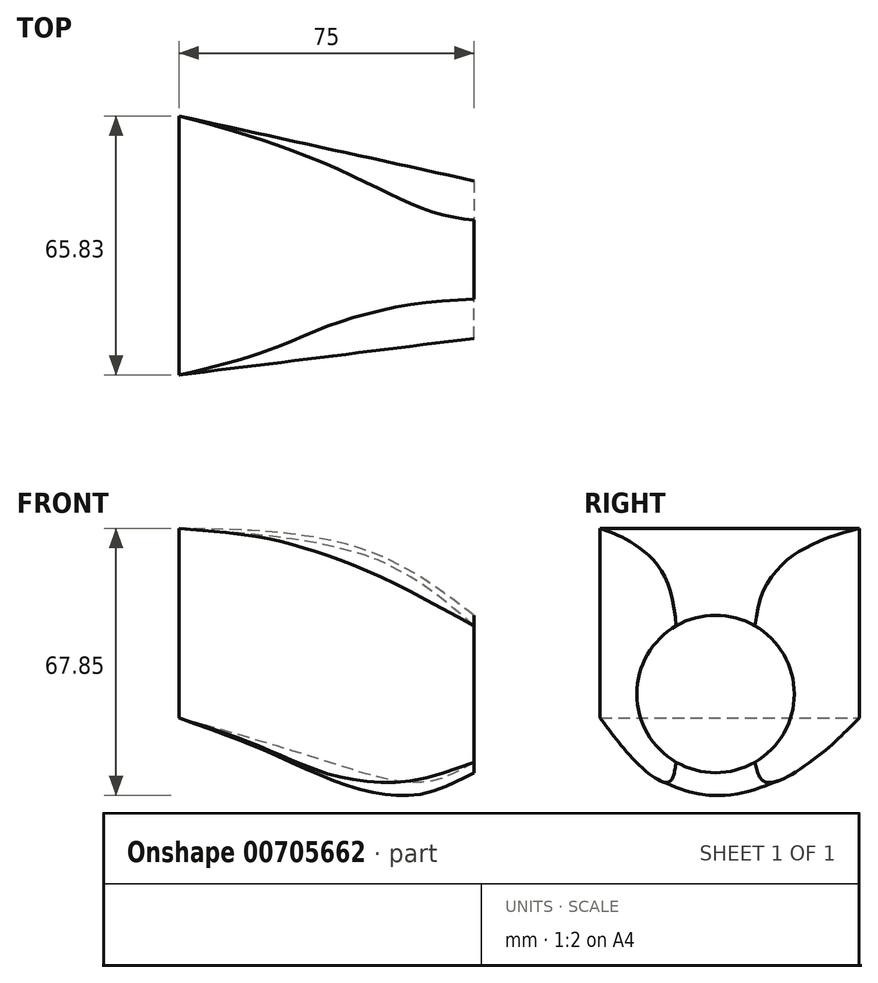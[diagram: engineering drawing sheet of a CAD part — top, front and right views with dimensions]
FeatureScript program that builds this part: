
annotation { "Feature Type Name" : "Feature", "Feature Type Description" : "" }
export const myFeature = defineFeature(function(context is Context, id is Id, definition is map)
    precondition{}
    {
        {
            var Q0;
            Q0=qCreatedBy(makeId("Right.planeOp"),FACE);
            var sketch = newSketch(context, id + "F0", { "sketchPlane" : qUnion([Q0])});
            skCircle(sketch, "E0", {"center": v(0, 0) * mm, "radius": 20 * mm});
            skSolve(sketch);
        }
        {
            var Q0;
            Q0=qCreatedBy(makeId("Right.planeOp"),FACE);
            cPlane(context, id + "F1", {"entities" : qUnion([Q0]), "cplaneType" : CPlaneType.OFFSET, "offset" : 75 * mm, "oppositeDirection" : true, "width" : 150 * mm, "height" : 150 * mm});
        }
        {
            var Q0;
            Q0=qCreatedBy(id+"F1.planeOp",FACE);
            var sketch = newSketch(context, id + "F2", { "sketchPlane" : qUnion([Q0])});
            skLineSegment(sketch, "E1.bottom", {"start": v(-29.32, -6.1) * mm, "end": v(36.51, -6.1) * mm});
            skLineSegment(sketch, "E1.top", {"start": v(-29.32, 42.04) * mm, "end": v(36.51, 42.04) * mm});
            skLineSegment(sketch, "E1.left", {"start": v(-29.32, -6.1) * mm, "end": v(-29.32, 42.04) * mm});
            skLineSegment(sketch, "E1.right", {"start": v(36.51, -6.1) * mm, "end": v(36.51, 42.04) * mm});
            skSolve(sketch);
        }
        {
            var Q0;
            Q0=qCreatedBy(makeId("Top.planeOp"),FACE);
            var sketch = newSketch(context, id + "F3", { "sketchPlane" : qUnion([Q0])});
            skLineSegment(sketch, "E2.0", {"start": v(-75, -29.32) * mm, "end": v(-75, 36.51) * mm});
            skLineSegment(sketch, "E3.0", {"start": v(0, 20) * mm, "end": v(0, -20) * mm});
            skPoint(sketch, "E4.2.internal.snap0", {"position": v(-75, 3.6) * mm});
            skFitSpline(sketch, "E4", {"points": [v(0, 0) * mm, v(-29.86, 13.64) * mm, v(-75, 0) * mm], "startDerivative": vector(-55.23, 57.64) * mm, "endDerivative": vector(-99.49, -65.42) * mm});
            skLineSegment(sketch, "E5", {"start": v(0, -20) * mm, "end": v(-75, -29.32) * mm});
            skLineSegment(sketch, "E6", {"start": v(0, 20) * mm, "end": v(-75, 36.51) * mm});
            skSolve(sketch);
        }
        {
            var Q0;
            Q0=sQuery(id+"F3.wireOp",EDGE,"E4");
            var Q1;
            Q1=makeQuery(id+"F0.imprint","IMPRINT",FACE,{"disambiguationData":[TD([[makeQuery(id+"F0.imprint","IMPRINT",EDGE,{"derivedFrom":sQuery(id+"F0.wireOp",EDGE,"E0")}),1.0]])]});
            var Q2;
            Q2=makeQuery(id+"F2.imprint","IMPRINT",FACE,{"disambiguationData":[TD([[makeQuery(id+"F2.imprint","IMPRINT",EDGE,{"derivedFrom":sQuery(id+"F2.wireOp",EDGE,"E1.bottom")}),1.0]])]});
            var Q3;
            Q3=sQuery(id+"F3.wireOp",EDGE,"E5");
            var Q4;
            Q4=sQuery(id+"F3.wireOp",EDGE,"E6");
            loft(context, id + "F4", {"addSections" : true, "spine" : qUnion([Q0]), "sectionCount" : 5, "addGuides" : true, "sheetProfilesArray" : [{ "sheetProfileEntities" : qUnion([Q1]) }, { "sheetProfileEntities" : qUnion([Q2]) }], "guidesArray" : [{ "guideEntities" : qUnion([Q3]), "guideDerivativeType" : LoftGuideDerivativeType.DEFAULT, "guideDerivativeMagnitude" : 1 }, { "guideEntities" : qUnion([Q4]), "guideDerivativeType" : LoftGuideDerivativeType.DEFAULT, "guideDerivativeMagnitude" : 1 }]});
        }
    });
